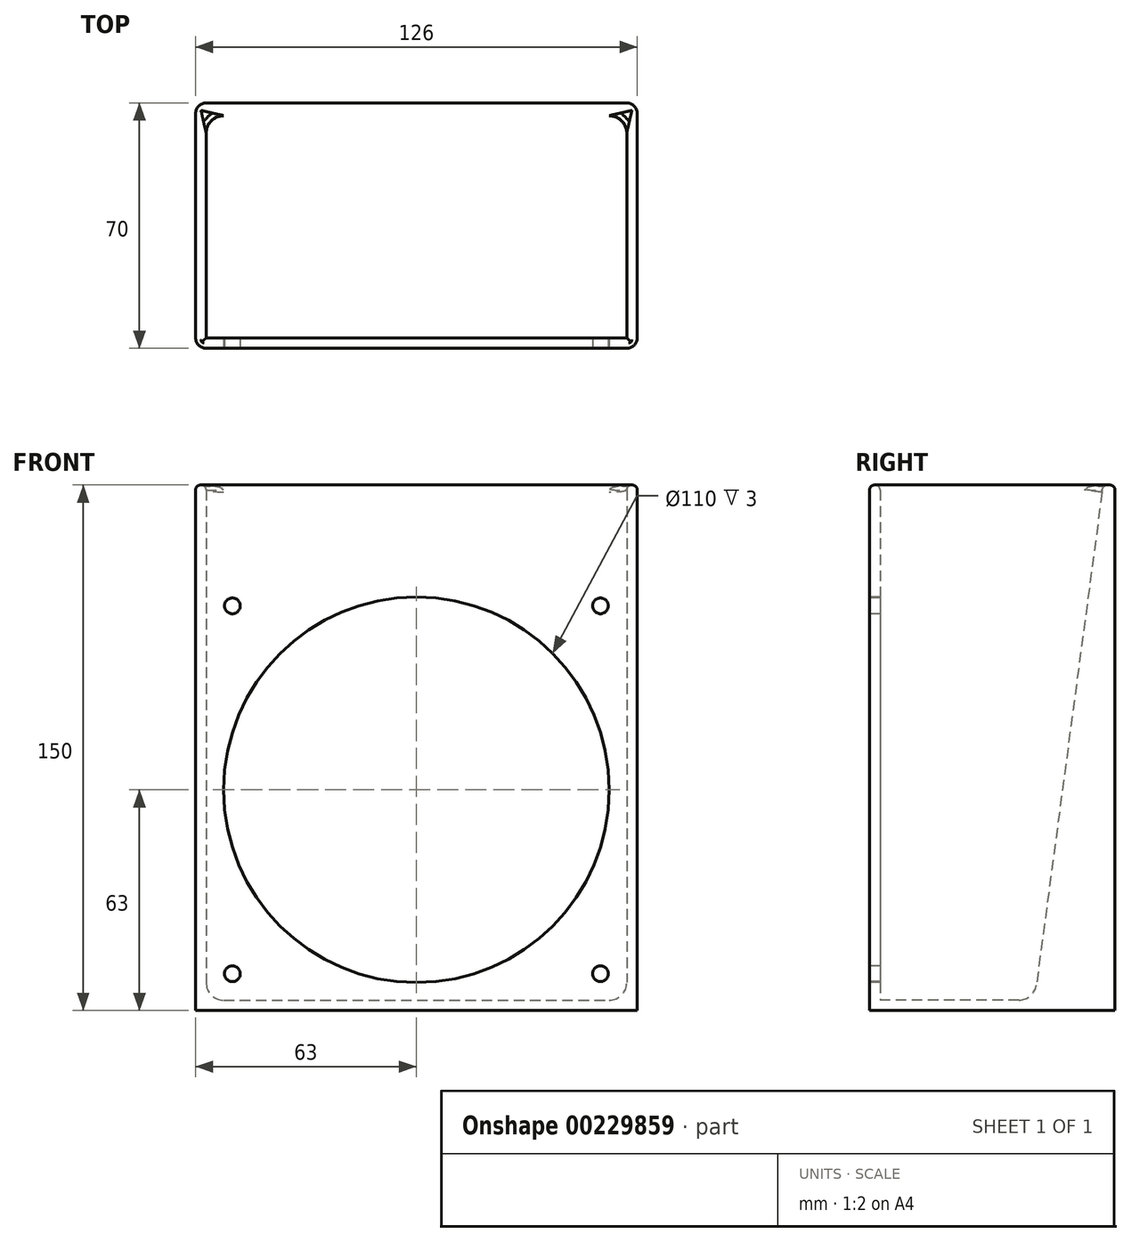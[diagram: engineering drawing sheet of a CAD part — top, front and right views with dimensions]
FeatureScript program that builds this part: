
annotation { "Feature Type Name" : "Feature", "Feature Type Description" : "" }
export const myFeature = defineFeature(function(context is Context, id is Id, definition is map)
    precondition{}
    {
        {
            var Q0;
            Q0=qCreatedBy(makeId("Top.planeOp"),FACE);
            var sketch = newSketch(context, id + "F0", { "sketchPlane" : qUnion([Q0])});
            skLineSegment(sketch, "E0.bottom", {"start": v(-63, 35) * mm, "end": v(63, 35) * mm});
            skLineSegment(sketch, "E0.top", {"start": v(-63, -35) * mm, "end": v(63, -35) * mm});
            skLineSegment(sketch, "E0.left", {"start": v(-63, 35) * mm, "end": v(-63, -35) * mm});
            skLineSegment(sketch, "E0.right", {"start": v(63, 35) * mm, "end": v(63, -35) * mm});
            skPoint(sketch, "E1", {"position": v(0, 35) * mm});
            skPoint(sketch, "E2", {"position": v(-63, 0) * mm});
            skSolve(sketch);
        }
        {
            var Q0;
            Q0=makeQuery(id+"F0.imprint","IMPRINT",FACE,{"disambiguationData":[TD([[makeQuery(id+"F0.imprint","IMPRINT",EDGE,{"derivedFrom":sQuery(id+"F0.wireOp",EDGE,"E0.bottom")}),-1.0]])]});
            extrude(context, id + "F1", {"entities" : qUnion([Q0]), "depth" : 150 * mm});
        }
        {
            var Q0;
            Q0=makeQuery(id+"F1.opExtrude","CAP_FACE",FACE,{"disambiguationData":[OSD([sQuery(id+"F0.wireOp",EDGE,"E0.bottom"),sQuery(id+"F0.wireOp",EDGE,"E0.top"),sQuery(id+"F0.wireOp",EDGE,"E0.left"),sQuery(id+"F0.wireOp",EDGE,"E0.right")])],"isStart":false});
            shell(context, id + "F2", {"entities" : qUnion([Q0]), "thickness" : 3 * mm});
        }
        {
            var Q0;
            Q0=makeQuery(id+"F1.opExtrude","SWEPT_FACE",FACE,{"disambiguationData":[OSD([sQuery(id+"F0.wireOp",EDGE,"E0.top")])]});
            var sketch = newSketch(context, id + "F3", { "sketchPlane" : qUnion([Q0])});
            skCircle(sketch, "E3", {"center": v(-52.5, 115.5) * mm, "radius": 2.25 * mm});
            skCircle(sketch, "E4", {"center": v(52.5, 115.5) * mm, "radius": 2.25 * mm});
            skCircle(sketch, "E5", {"center": v(52.5, 10.5) * mm, "radius": 2.25 * mm});
            skCircle(sketch, "E6", {"center": v(-52.5, 10.5) * mm, "radius": 2.25 * mm});
            skLineSegment(sketch, "E7", {"start": v(-52.5, 115.5) * mm, "end": v(52.5, 115.5) * mm});
            skLineSegment(sketch, "E8", {"start": v(-52.5, 115.5) * mm, "end": v(-52.5, 10.5) * mm});
            skPoint(sketch, "E9", {"position": v(0, 115.5) * mm});
            skPoint(sketch, "E10", {"position": v(-52.5, 63) * mm});
            skCircle(sketch, "E11", {"center": v(0, 63) * mm, "radius": 55 * mm});
            skSolve(sketch);
        }
        {
            var Q0;
            {var subQ0=sQuery(id+"F3.wireOp",EDGE,"E7");var subQ1=sQuery(id+"F3.wireOp",EDGE,"E3");var subQ2=makeQuery(id+"F3.imprint","INTERSECT",VERTEX,{"derivedFrom":[subQ1,subQ0]});Q0=makeQuery(id+"F3.imprint","IMPRINT",FACE,{"disambiguationData":[TD([[makeQuery(id+"F3.imprint","IMPRINT",EDGE,{"disambiguationData":[TD([[subQ2,-1.0]])],"derivedFrom":subQ1}),1.0]])]});}
            var Q1;
            {var subQ0=sQuery(id+"F3.wireOp",EDGE,"E7");var subQ1=sQuery(id+"F3.wireOp",EDGE,"E3");var subQ2=makeQuery(id+"F3.imprint","INTERSECT",VERTEX,{"derivedFrom":[subQ1,subQ0]});Q1=makeQuery(id+"F3.imprint","IMPRINT",FACE,{"disambiguationData":[TD([[makeQuery(id+"F3.imprint","IMPRINT",EDGE,{"disambiguationData":[TD([[subQ2,1.0]])],"derivedFrom":subQ1}),1.0]])]});}
            var Q2;
            {var subQ0=sQuery(id+"F3.wireOp",EDGE,"E11");var subQ1=sQuery(id+"F3.wireOp",EDGE,"E7");var subQ2=makeQuery(id+"F3.imprint","INTERSECT",VERTEX,{"disambiguationData":[OD(0.0)],"derivedFrom":[subQ1,subQ0]});Q2=makeQuery(id+"F3.imprint","IMPRINT",FACE,{"disambiguationData":[TD([[makeQuery(id+"F3.imprint","IMPRINT",EDGE,{"disambiguationData":[TD([[subQ2,1.0]])],"derivedFrom":subQ1}),-1.0]])]});}
            var Q3;
            {var subQ0=sQuery(id+"F3.wireOp",EDGE,"E11");var subQ1=sQuery(id+"F3.wireOp",EDGE,"E7");var subQ2=makeQuery(id+"F3.imprint","INTERSECT",VERTEX,{"disambiguationData":[OD(0.0)],"derivedFrom":[subQ1,subQ0]});Q3=makeQuery(id+"F3.imprint","IMPRINT",FACE,{"disambiguationData":[TD([[makeQuery(id+"F3.imprint","IMPRINT",EDGE,{"disambiguationData":[TD([[subQ2,1.0]])],"derivedFrom":subQ1}),1.0]])]});}
            var Q4;
            {var subQ0=sQuery(id+"F3.wireOp",EDGE,"E11");var subQ1=sQuery(id+"F3.wireOp",EDGE,"E8");var subQ2=makeQuery(id+"F3.imprint","INTERSECT",VERTEX,{"disambiguationData":[OD(0.0)],"derivedFrom":[subQ1,subQ0]});Q4=makeQuery(id+"F3.imprint","IMPRINT",FACE,{"disambiguationData":[TD([[makeQuery(id+"F3.imprint","IMPRINT",EDGE,{"disambiguationData":[TD([[subQ2,1.0]])],"derivedFrom":subQ1}),-1.0]])]});}
            var Q5;
            Q5=makeQuery(id+"F3.imprint","IMPRINT",FACE,{"disambiguationData":[TD([[makeQuery(id+"F3.imprint","IMPRINT",EDGE,{"derivedFrom":sQuery(id+"F3.wireOp",EDGE,"E6")}),1.0]])]});
            var Q6;
            Q6=makeQuery(id+"F3.imprint","IMPRINT",FACE,{"disambiguationData":[TD([[makeQuery(id+"F3.imprint","IMPRINT",EDGE,{"derivedFrom":sQuery(id+"F3.wireOp",EDGE,"E5")}),1.0]])]});
            var Q7;
            Q7=makeQuery(id+"F3.imprint","IMPRINT",FACE,{"disambiguationData":[TD([[makeQuery(id+"F3.imprint","IMPRINT",EDGE,{"derivedFrom":sQuery(id+"F3.wireOp",EDGE,"E4")}),1.0]])]});
            extrude(context, id + "F4", {"entities" : qUnion([Q0, Q1, Q2, Q3, Q4, Q5, Q6, Q7]), "operationType" : NewBodyOperationType.REMOVE, "endBound" : BoundingType.UP_TO_NEXT, "oppositeDirection" : true, "depth" : 25 * mm});
        }
        {
            var Q0;
            {var subQ0=sQuery(id+"F0.wireOp",EDGE,"E0.bottom");Q0=makeQuery(id+"F2.opShell","OFFSET_EDGE",EDGE,{"disambiguationData":[OSD([subQ0]),TDD([makeQuery(id+"F1.opExtrude","CAP_EDGE",EDGE,{"disambiguationData":[OSD([subQ0])],"isStart":true})])]});}
            chamfer(context, id + "F5", {"entities" : qUnion([Q0]), "chamferType" : ChamferType.TWO_OFFSETS, "width1" : 150 * mm, "oppositeDirection" : false, "width2" : 20 * mm, "tangentPropagation" : true});
        }
        {
            var Q0;
            Q0=makeQuery(id+"F1.opExtrude","SWEPT_EDGE",EDGE,{"disambiguationData":[OSD([sQuery(id+"F0.wireOp",EDGE,"E0.top"),sQuery(id+"F0.wireOp",EDGE,"E0.left")])]});
            var Q1;
            Q1=makeQuery(id+"F1.opExtrude","SWEPT_EDGE",EDGE,{"disambiguationData":[OSD([sQuery(id+"F0.wireOp",EDGE,"E0.top"),sQuery(id+"F0.wireOp",EDGE,"E0.right")])]});
            var Q2;
            Q2=makeQuery(id+"F1.opExtrude","SWEPT_EDGE",EDGE,{"disambiguationData":[OSD([sQuery(id+"F0.wireOp",EDGE,"E0.bottom"),sQuery(id+"F0.wireOp",EDGE,"E0.left")])]});
            var Q3;
            Q3=makeQuery(id+"F1.opExtrude","SWEPT_EDGE",EDGE,{"disambiguationData":[OSD([sQuery(id+"F0.wireOp",EDGE,"E0.bottom"),sQuery(id+"F0.wireOp",EDGE,"E0.right")])]});
            fillet(context, id + "F6", {"entities" : qUnion([Q0, Q1, Q2, Q3]), "radius" : 3 * mm, "tangentPropagation" : true, "allowEdgeOverflow" : false});
        }
        {
            var Q0;
            {var subQ0=sQuery(id+"F0.wireOp",EDGE,"E0.bottom");Q0=makeQuery(id+"F5.opChamfer","BLEND_EDGE",EDGE,{"blendedFrom":[makeQuery(id+"F2.opShell","OFFSET_EDGE",EDGE,{"disambiguationData":[OSD([subQ0]),TDD([makeQuery(id+"F1.opExtrude","CAP_EDGE",EDGE,{"disambiguationData":[OSD([subQ0])],"isStart":true})])]}),makeQuery(id+"F1.opExtrude","CAP_FACE",FACE,{"disambiguationData":[OSD([subQ0,sQuery(id+"F0.wireOp",EDGE,"E0.top"),sQuery(id+"F0.wireOp",EDGE,"E0.left"),sQuery(id+"F0.wireOp",EDGE,"E0.right")])],"isStart":false})],"blendedInto":[makeQuery(id+"F1.opExtrude","CAP_FACE",FACE,{"disambiguationData":[OSD([subQ0,sQuery(id+"F0.wireOp",EDGE,"E0.top"),sQuery(id+"F0.wireOp",EDGE,"E0.left"),sQuery(id+"F0.wireOp",EDGE,"E0.right")])],"isStart":false})]});}
            var Q1;
            {var subQ0=sQuery(id+"F0.wireOp",EDGE,"E0.top");Q1=makeQuery(id+"F2.opShell","OFFSET_EDGE",EDGE,{"disambiguationData":[OSD([subQ0]),TDD([makeQuery(id+"F1.opExtrude","CAP_EDGE",EDGE,{"disambiguationData":[OSD([subQ0])],"isStart":false})])]});}
            var Q2;
            {var subQ0=sQuery(id+"F0.wireOp",EDGE,"E0.right");Q2=makeQuery(id+"F2.opShell","OFFSET_EDGE",EDGE,{"disambiguationData":[OSD([subQ0]),TDD([makeQuery(id+"F1.opExtrude","CAP_EDGE",EDGE,{"disambiguationData":[OSD([subQ0])],"isStart":false})])]});}
            var Q3;
            {var subQ0=sQuery(id+"F0.wireOp",EDGE,"E0.left");Q3=makeQuery(id+"F2.opShell","OFFSET_EDGE",EDGE,{"disambiguationData":[OSD([subQ0]),TDD([makeQuery(id+"F1.opExtrude","CAP_EDGE",EDGE,{"disambiguationData":[OSD([subQ0])],"isStart":false})])]});}
            var Q4;
            Q4=makeQuery(id+"F1.opExtrude","CAP_EDGE",EDGE,{"disambiguationData":[OSD([sQuery(id+"F0.wireOp",EDGE,"E0.left")])],"isStart":false});
            fillet(context, id + "F7", {"entities" : qUnion([Q0, Q1, Q2, Q3, Q4]), "radius" : 1.45 * mm, "tangentPropagation" : true, "allowEdgeOverflow" : false});
        }
        {
            var Q0;
            {var subQ0=sQuery(id+"F0.wireOp",EDGE,"E0.bottom");Q0=makeQuery(id+"F5.opChamfer","BLEND_EDGE",EDGE,{"blendedFrom":[makeQuery(id+"F2.opShell","OFFSET_EDGE",EDGE,{"disambiguationData":[OSD([subQ0]),TDD([makeQuery(id+"F1.opExtrude","CAP_EDGE",EDGE,{"disambiguationData":[OSD([subQ0])],"isStart":true})])]}),makeQuery(id+"F2.opShell","OFFSET_FACE",FACE,{"disambiguationData":[OSD([sQuery(id+"F0.wireOp",EDGE,"E0.left")])]})],"blendedInto":[makeQuery(id+"F2.opShell","OFFSET_FACE",FACE,{"disambiguationData":[OSD([sQuery(id+"F0.wireOp",EDGE,"E0.left")])]})]});}
            var Q1;
            {var subQ0=sQuery(id+"F0.wireOp",EDGE,"E0.bottom");Q1=makeQuery(id+"F5.opChamfer","BLEND_EDGE",EDGE,{"blendedFrom":[makeQuery(id+"F2.opShell","OFFSET_EDGE",EDGE,{"disambiguationData":[OSD([subQ0]),TDD([makeQuery(id+"F1.opExtrude","CAP_EDGE",EDGE,{"disambiguationData":[OSD([subQ0])],"isStart":true})])]}),makeQuery(id+"F2.opShell","OFFSET_FACE",FACE,{"disambiguationData":[OSD([sQuery(id+"F0.wireOp",EDGE,"E0.right")])]})],"blendedInto":[makeQuery(id+"F2.opShell","OFFSET_FACE",FACE,{"disambiguationData":[OSD([sQuery(id+"F0.wireOp",EDGE,"E0.right")])]})]});}
            var Q2;
            {var subQ0=sQuery(id+"F0.wireOp",EDGE,"E0.bottom");Q2=makeQuery(id+"F5.opChamfer","BLEND_EDGE",EDGE,{"blendedFrom":[makeQuery(id+"F2.opShell","OFFSET_EDGE",EDGE,{"disambiguationData":[OSD([subQ0]),TDD([makeQuery(id+"F1.opExtrude","CAP_EDGE",EDGE,{"disambiguationData":[OSD([subQ0])],"isStart":true})])]}),makeQuery(id+"F2.opShell","OFFSET_FACE",FACE,{"disambiguationData":[OSD([subQ0,sQuery(id+"F0.wireOp",EDGE,"E0.top"),sQuery(id+"F0.wireOp",EDGE,"E0.left"),sQuery(id+"F0.wireOp",EDGE,"E0.right")])]})],"blendedInto":[makeQuery(id+"F2.opShell","OFFSET_FACE",FACE,{"disambiguationData":[OSD([subQ0,sQuery(id+"F0.wireOp",EDGE,"E0.top"),sQuery(id+"F0.wireOp",EDGE,"E0.left"),sQuery(id+"F0.wireOp",EDGE,"E0.right")])]})]});}
            var Q3;
            {var subQ0=sQuery(id+"F0.wireOp",EDGE,"E0.left");Q3=makeQuery(id+"F2.opShell","OFFSET_EDGE",EDGE,{"disambiguationData":[OSD([subQ0]),TDD([makeQuery(id+"F1.opExtrude","CAP_EDGE",EDGE,{"disambiguationData":[OSD([subQ0])],"isStart":true})])]});}
            var Q4;
            {var subQ0=sQuery(id+"F0.wireOp",EDGE,"E0.right");Q4=makeQuery(id+"F2.opShell","OFFSET_EDGE",EDGE,{"disambiguationData":[OSD([subQ0]),TDD([makeQuery(id+"F1.opExtrude","CAP_EDGE",EDGE,{"disambiguationData":[OSD([subQ0])],"isStart":true})])]});}
            fillet(context, id + "F8", {"entities" : qUnion([Q0, Q1, Q2, Q3, Q4]), "radius" : 5 * mm, "tangentPropagation" : true, "allowEdgeOverflow" : false});
        }
    });
